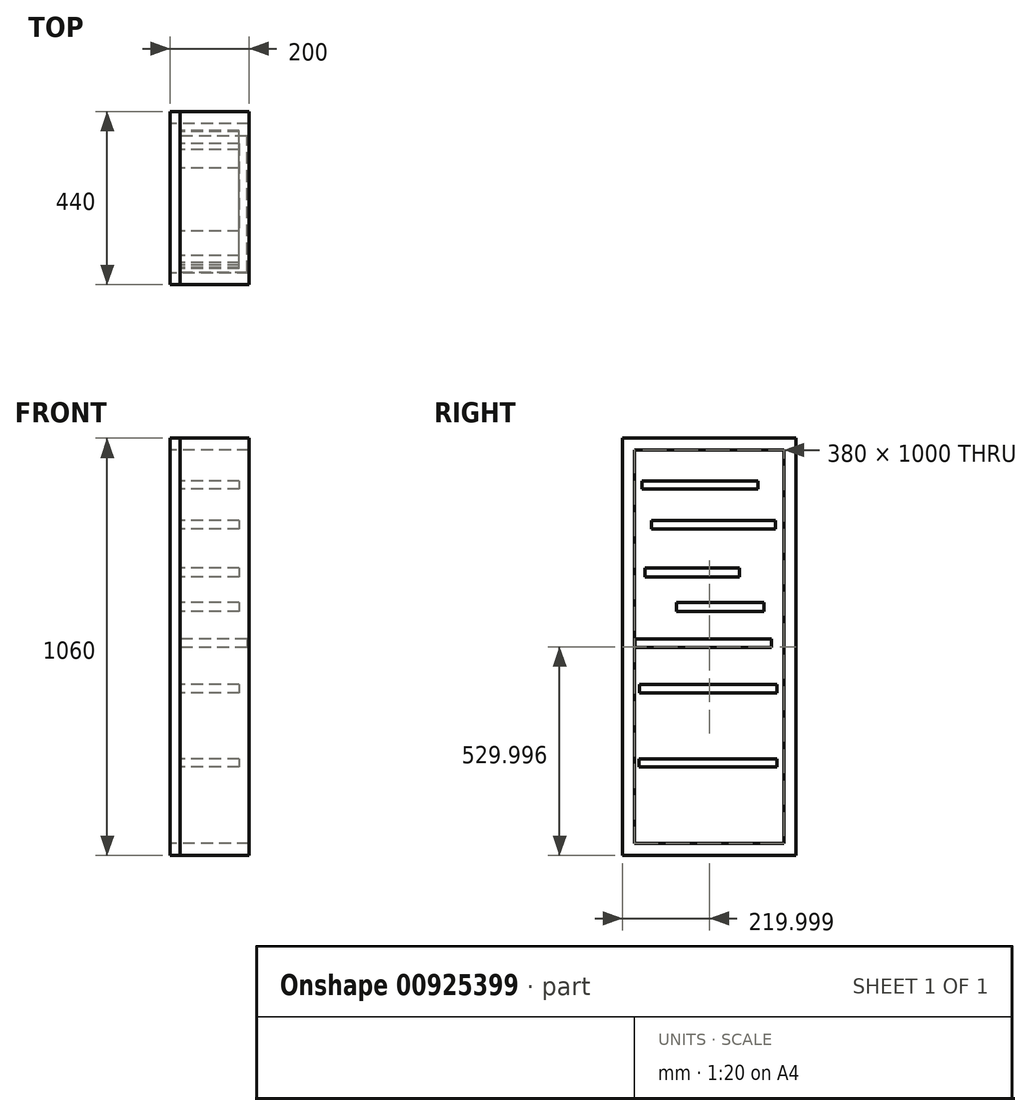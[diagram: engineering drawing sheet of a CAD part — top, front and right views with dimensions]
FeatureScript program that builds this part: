
annotation { "Feature Type Name" : "Feature", "Feature Type Description" : "" }
export const myFeature = defineFeature(function(context is Context, id is Id, definition is map)
    precondition{}
    {
        {
            var Q0;
            Q0=qCreatedBy(makeId("Right.planeOp"),FACE);
            var sketch = newSketch(context, id + "F0", { "sketchPlane" : qUnion([Q0])});
            skLineSegment(sketch, "E0.bottom", {"start": v(-454.81, 479.7) * mm, "end": v(-74.81, 479.7) * mm});
            skLineSegment(sketch, "E0.top", {"start": v(-454.81, -520.3) * mm, "end": v(-74.81, -520.3) * mm});
            skLineSegment(sketch, "E0.left", {"start": v(-454.81, 479.7) * mm, "end": v(-454.81, -520.3) * mm});
            skLineSegment(sketch, "E0.right", {"start": v(-74.81, 479.7) * mm, "end": v(-74.81, -520.3) * mm});
            skLineSegment(sketch, "E1.bottom", {"start": v(-74.81, 479.7) * mm, "end": v(-44.81, 479.7) * mm});
            skLineSegment(sketch, "E1.top", {"start": v(-74.81, -520.3) * mm, "end": v(-44.81, -520.3) * mm});
            skLineSegment(sketch, "E1.right", {"start": v(-44.81, 479.7) * mm, "end": v(-44.81, -520.3) * mm});
            skLineSegment(sketch, "E2.bottom", {"start": v(-454.81, 479.7) * mm, "end": v(-484.81, 479.7) * mm});
            skLineSegment(sketch, "E2.top", {"start": v(-454.81, -520.3) * mm, "end": v(-484.81, -520.3) * mm});
            skLineSegment(sketch, "E2.right", {"start": v(-484.81, 479.7) * mm, "end": v(-484.81, -520.3) * mm});
            skLineSegment(sketch, "E3.bottom", {"start": v(-484.81, 479.7) * mm, "end": v(-44.81, 479.7) * mm});
            skLineSegment(sketch, "E3.top", {"start": v(-484.81, 509.7) * mm, "end": v(-44.81, 509.7) * mm});
            skLineSegment(sketch, "E3.left", {"start": v(-484.81, 479.7) * mm, "end": v(-484.81, 509.7) * mm});
            skLineSegment(sketch, "E3.right", {"start": v(-44.81, 479.7) * mm, "end": v(-44.81, 509.7) * mm});
            skLineSegment(sketch, "E4.bottom", {"start": v(-484.81, -520.3) * mm, "end": v(-44.81, -520.3) * mm});
            skLineSegment(sketch, "E4.top", {"start": v(-484.81, -550.3) * mm, "end": v(-44.81, -550.3) * mm});
            skLineSegment(sketch, "E4.left", {"start": v(-484.81, -520.3) * mm, "end": v(-484.81, -550.3) * mm});
            skLineSegment(sketch, "E4.right", {"start": v(-44.81, -520.3) * mm, "end": v(-44.81, -550.3) * mm});
            skSolve(sketch);
        }
        {
            var Q0;
            Q0=makeQuery(id+"F0.imprint","IMPRINT",FACE,{"disambiguationData":[TD([[makeQuery(id+"F0.imprint","IMPRINT",EDGE,{"derivedFrom":sQuery(id+"F0.wireOp",EDGE,"E2.bottom")}),1.0]])]});
            var Q1;
            Q1=makeQuery(id+"F0.imprint","IMPRINT",FACE,{"disambiguationData":[TD([[makeQuery(id+"F0.imprint","IMPRINT",EDGE,{"derivedFrom":sQuery(id+"F0.wireOp",EDGE,"E1.bottom")}),-1.0]])]});
            var Q2;
            Q2=makeQuery(id+"F0.imprint","IMPRINT",FACE,{"disambiguationData":[TD([[makeQuery(id+"F0.imprint","IMPRINT",EDGE,{"derivedFrom":sQuery(id+"F0.wireOp",EDGE,"E0.left")}),-1.0]])]});
            var Q3;
            Q3=makeQuery(id+"F0.imprint","IMPRINT",FACE,{"disambiguationData":[TD([[makeQuery(id+"F0.imprint","IMPRINT",EDGE,{"derivedFrom":sQuery(id+"F0.wireOp",EDGE,"E0.bottom")}),1.0]])]});
            var Q4;
            Q4=makeQuery(id+"F0.imprint","IMPRINT",FACE,{"disambiguationData":[TD([[makeQuery(id+"F0.imprint","IMPRINT",EDGE,{"derivedFrom":sQuery(id+"F0.wireOp",EDGE,"E0.right")}),1.0]])]});
            var Q5;
            Q5=makeQuery(id+"F0.imprint","IMPRINT",FACE,{"disambiguationData":[TD([[makeQuery(id+"F0.imprint","IMPRINT",EDGE,{"derivedFrom":sQuery(id+"F0.wireOp",EDGE,"E0.top")}),-1.0]])]});
            extrude(context, id + "F1", {"entities" : qUnion([Q0, Q1, Q2, Q3, Q4, Q5]), "depth" : 200 * mm, "offsetDistance" : 25 * mm});
        }
        {
            var Q0;
            {Q0=qUnion([makeQuery(id+"F0.imprint","IMPRINT",FACE,{"disambiguationData":[TD([[makeQuery(id+"F0.imprint","IMPRINT",EDGE,{"derivedFrom":sQuery(id+"F0.wireOp",EDGE,"E0.right")}),1.0]])]}),makeQuery(id+"F0.imprint","IMPRINT",FACE,{"disambiguationData":[TD([[makeQuery(id+"F0.imprint","IMPRINT",EDGE,{"derivedFrom":sQuery(id+"F0.wireOp",EDGE,"E0.bottom")}),1.0]])]}),makeQuery(id+"F0.imprint","IMPRINT",FACE,{"disambiguationData":[TD([[makeQuery(id+"F0.imprint","IMPRINT",EDGE,{"derivedFrom":sQuery(id+"F0.wireOp",EDGE,"E0.top")}),-1.0]])]}),makeQuery(id+"F0.imprint","IMPRINT",FACE,{"disambiguationData":[TD([[makeQuery(id+"F0.imprint","IMPRINT",EDGE,{"derivedFrom":sQuery(id+"F0.wireOp",EDGE,"E0.left")}),-1.0]])]})]);}
            var Q1;
            Q1=makeQuery(id+"F0.imprint","IMPRINT",FACE,{"disambiguationData":[TD([[makeQuery(id+"F0.imprint","IMPRINT",EDGE,{"derivedFrom":sQuery(id+"F0.wireOp",EDGE,"E0.bottom")}),-1.0]])]});
            extrude(context, id + "F2", {"entities" : qUnion([Q0, Q1]), "depth" : 25 * mm, "offsetDistance" : 25 * mm});
        }
        {
            var Q0;
            Q0=qCreatedBy(makeId("Right.planeOp"),FACE);
            var sketch = newSketch(context, id + "F3", { "sketchPlane" : qUnion([Q0])});
            skLineSegment(sketch, "E5.bottom", {"start": v(-456.7, 504.2) * mm, "end": v(-266.7, 504.2) * mm});
            skLineSegment(sketch, "E5.top", {"start": v(-456.7, -495.8) * mm, "end": v(-266.7, -495.8) * mm});
            skLineSegment(sketch, "E5.left", {"start": v(-456.7, 504.2) * mm, "end": v(-456.7, -495.8) * mm});
            skLineSegment(sketch, "E5.right", {"start": v(-266.7, 504.2) * mm, "end": v(-266.7, -495.8) * mm});
            skSolve(sketch);
        }
        {
            var Q0;
            Q0=makeQuery(id+"F3.imprint","IMPRINT",FACE,{"disambiguationData":[TD([[makeQuery(id+"F3.imprint","IMPRINT",EDGE,{"derivedFrom":sQuery(id+"F3.wireOp",EDGE,"E5.bottom")}),-1.0]])]});
            extrude(context, id + "F4", {"entities" : qUnion([Q0]), "depth" : 25 * mm, "offsetDistance" : 25 * mm});
        }
        {
            var Q0;
            Q0=makeQuery(id+"F2.opExtrude","CAP_FACE",FACE,{"disambiguationData":[OSD([sQuery(id+"F0.wireOp",EDGE,"E1.right"),sQuery(id+"F0.wireOp",EDGE,"E2.right"),sQuery(id+"F0.wireOp",EDGE,"E3.top"),sQuery(id+"F0.wireOp",EDGE,"E3.left"),sQuery(id+"F0.wireOp",EDGE,"E3.right"),sQuery(id+"F0.wireOp",EDGE,"E4.top"),sQuery(id+"F0.wireOp",EDGE,"E4.left"),sQuery(id+"F0.wireOp",EDGE,"E4.right")])],"isStart":false});
            var sketch = newSketch(context, id + "F5", { "sketchPlane" : qUnion([Q0])});
            skLineSegment(sketch, "E6.bottom", {"start": v(-411.2, 300.74) * mm, "end": v(-96.11, 300.74) * mm});
            skLineSegment(sketch, "E6.top", {"start": v(-411.2, 278.96) * mm, "end": v(-96.11, 278.96) * mm});
            skLineSegment(sketch, "E6.left", {"start": v(-411.2, 300.74) * mm, "end": v(-411.2, 278.96) * mm});
            skLineSegment(sketch, "E6.right", {"start": v(-96.11, 300.74) * mm, "end": v(-96.11, 278.96) * mm});
            skLineSegment(sketch, "E7.bottom", {"start": v(-96.11, 278.96) * mm, "end": v(-126.24, 278.96) * mm});
            skLineSegment(sketch, "E7.top", {"start": v(-96.11, 69.49) * mm, "end": v(-126.24, 69.49) * mm});
            skLineSegment(sketch, "E7.left", {"start": v(-96.11, 278.96) * mm, "end": v(-96.11, 69.49) * mm});
            skLineSegment(sketch, "E7.right", {"start": v(-126.24, 278.96) * mm, "end": v(-126.24, 69.49) * mm});
            skLineSegment(sketch, "E8.bottom", {"start": v(-126.24, 69.49) * mm, "end": v(-348.13, 69.49) * mm});
            skLineSegment(sketch, "E8.top", {"start": v(-126.24, 92.75) * mm, "end": v(-348.13, 92.75) * mm});
            skLineSegment(sketch, "E8.left", {"start": v(-126.24, 69.49) * mm, "end": v(-126.24, 92.75) * mm});
            skLineSegment(sketch, "E8.right", {"start": v(-348.13, 69.49) * mm, "end": v(-348.13, 92.75) * mm});
            skLineSegment(sketch, "E9.bottom", {"start": v(-427.88, 179.74) * mm, "end": v(-188.42, 179.74) * mm});
            skLineSegment(sketch, "E9.top", {"start": v(-427.88, 156.71) * mm, "end": v(-188.42, 156.71) * mm});
            skLineSegment(sketch, "E9.left", {"start": v(-427.88, 179.74) * mm, "end": v(-427.88, 156.71) * mm});
            skLineSegment(sketch, "E9.right", {"start": v(-188.42, 179.74) * mm, "end": v(-188.42, 156.71) * mm});
            skLineSegment(sketch, "E10.bottom", {"start": v(-443.23, -305.4) * mm, "end": v(-92.8, -305.4) * mm});
            skLineSegment(sketch, "E10.top", {"start": v(-443.23, -326) * mm, "end": v(-92.8, -326) * mm});
            skLineSegment(sketch, "E10.left", {"start": v(-443.23, -305.4) * mm, "end": v(-443.23, -326) * mm});
            skLineSegment(sketch, "E10.right", {"start": v(-92.8, -305.4) * mm, "end": v(-92.8, -326) * mm});
            skLineSegment(sketch, "E11.bottom", {"start": v(-441.48, -115.71) * mm, "end": v(-92.8, -115.71) * mm});
            skLineSegment(sketch, "E11.top", {"start": v(-441.48, -137.12) * mm, "end": v(-92.8, -137.12) * mm});
            skLineSegment(sketch, "E11.left", {"start": v(-441.48, -115.71) * mm, "end": v(-441.48, -137.12) * mm});
            skLineSegment(sketch, "E11.right", {"start": v(-92.8, -115.71) * mm, "end": v(-92.8, -137.12) * mm});
            skLineSegment(sketch, "E12.bottom", {"start": v(-435.32, 401.23) * mm, "end": v(-141.45, 401.23) * mm});
            skLineSegment(sketch, "E12.top", {"start": v(-435.32, 380.2) * mm, "end": v(-141.45, 380.2) * mm});
            skLineSegment(sketch, "E12.left", {"start": v(-435.32, 401.23) * mm, "end": v(-435.32, 380.2) * mm});
            skLineSegment(sketch, "E12.right", {"start": v(-141.45, 401.23) * mm, "end": v(-141.45, 380.2) * mm});
            skLineSegment(sketch, "E13.bottom", {"start": v(-453.7, 17.37) * mm, "end": v(-113.46, 17.37) * mm});
            skLineSegment(sketch, "E13.top", {"start": v(-453.7, -9.88) * mm, "end": v(-113.46, -9.88) * mm});
            skLineSegment(sketch, "E13.left", {"start": v(-453.7, 17.37) * mm, "end": v(-453.7, -9.88) * mm});
            skLineSegment(sketch, "E13.right", {"start": v(-113.46, 17.37) * mm, "end": v(-113.46, -9.88) * mm});
            skSolve(sketch);
        }
        {
            var Q0;
            Q0=makeQuery(id+"F5.imprint","IMPRINT",FACE,{"disambiguationData":[TD([[makeQuery(id+"F5.imprint","IMPRINT",EDGE,{"derivedFrom":sQuery(id+"F5.wireOp",EDGE,"E12.bottom")}),-1.0]])]});
            var Q1;
            Q1=makeQuery(id+"F5.imprint","IMPRINT",FACE,{"disambiguationData":[TD([[makeQuery(id+"F5.imprint","IMPRINT",EDGE,{"derivedFrom":sQuery(id+"F5.wireOp",EDGE,"E6.bottom")}),-1.0]])]});
            var Q2;
            Q2=makeQuery(id+"F5.imprint","IMPRINT",FACE,{"disambiguationData":[TD([[makeQuery(id+"F5.imprint","IMPRINT",EDGE,{"derivedFrom":sQuery(id+"F5.wireOp",EDGE,"E9.bottom")}),-1.0]])]});
            var Q3;
            Q3=makeQuery(id+"F5.imprint","IMPRINT",FACE,{"disambiguationData":[TD([[makeQuery(id+"F5.imprint","IMPRINT",EDGE,{"derivedFrom":sQuery(id+"F5.wireOp",EDGE,"E8.bottom")}),-1.0]])]});
            var Q4;
            Q4=makeQuery(id+"F5.imprint","IMPRINT",FACE,{"disambiguationData":[TD([[makeQuery(id+"F5.imprint","IMPRINT",EDGE,{"derivedFrom":sQuery(id+"F5.wireOp",EDGE,"E7.bottom")}),1.0]])]});
            var Q5;
            Q5=makeQuery(id+"F5.imprint","IMPRINT",FACE,{"disambiguationData":[TD([[makeQuery(id+"F5.imprint","IMPRINT",EDGE,{"derivedFrom":sQuery(id+"F5.wireOp",EDGE,"E11.bottom")}),-1.0]])]});
            var Q6;
            Q6=makeQuery(id+"F5.imprint","IMPRINT",FACE,{"disambiguationData":[TD([[makeQuery(id+"F5.imprint","IMPRINT",EDGE,{"derivedFrom":sQuery(id+"F5.wireOp",EDGE,"E10.bottom")}),-1.0]])]});
            extrude(context, id + "F6", {"entities" : qUnion([Q0, Q1, Q2, Q3, Q4, Q5, Q6]), "operationType" : NewBodyOperationType.ADD, "depth" : 150 * mm, "offsetDistance" : 25 * mm});
        }
        {
            var Q0;
            Q0=makeQuery(id+"F2.opExtrude","CAP_FACE",FACE,{"disambiguationData":[OSD([sQuery(id+"F0.wireOp",EDGE,"E1.right"),sQuery(id+"F0.wireOp",EDGE,"E2.right"),sQuery(id+"F0.wireOp",EDGE,"E3.top"),sQuery(id+"F0.wireOp",EDGE,"E3.left"),sQuery(id+"F0.wireOp",EDGE,"E3.right"),sQuery(id+"F0.wireOp",EDGE,"E4.top"),sQuery(id+"F0.wireOp",EDGE,"E4.left"),sQuery(id+"F0.wireOp",EDGE,"E4.right")])],"isStart":false});
            var sketch = newSketch(context, id + "F7", { "sketchPlane" : qUnion([Q0])});
            skLineSegment(sketch, "E14.bottom", {"start": v(-453.65, 0) * mm, "end": v(-107.31, 0) * mm});
            skLineSegment(sketch, "E14.top", {"start": v(-453.65, -21.25) * mm, "end": v(-107.31, -21.25) * mm});
            skLineSegment(sketch, "E14.left", {"start": v(-453.65, 0) * mm, "end": v(-453.65, -21.25) * mm});
            skLineSegment(sketch, "E14.right", {"start": v(-107.31, 0) * mm, "end": v(-107.31, -21.25) * mm});
            skSolve(sketch);
        }
        {
            var Q0;
            Q0=makeQuery(id+"F7.imprint","IMPRINT",FACE,{"disambiguationData":[TD([[makeQuery(id+"F7.imprint","IMPRINT",EDGE,{"derivedFrom":sQuery(id+"F7.wireOp",EDGE,"E14.bottom")}),-1.0]])]});
            extrude(context, id + "F8", {"entities" : qUnion([Q0]), "operationType" : NewBodyOperationType.ADD, "depth" : 170 * mm, "offsetDistance" : 25 * mm});
        }
    });
